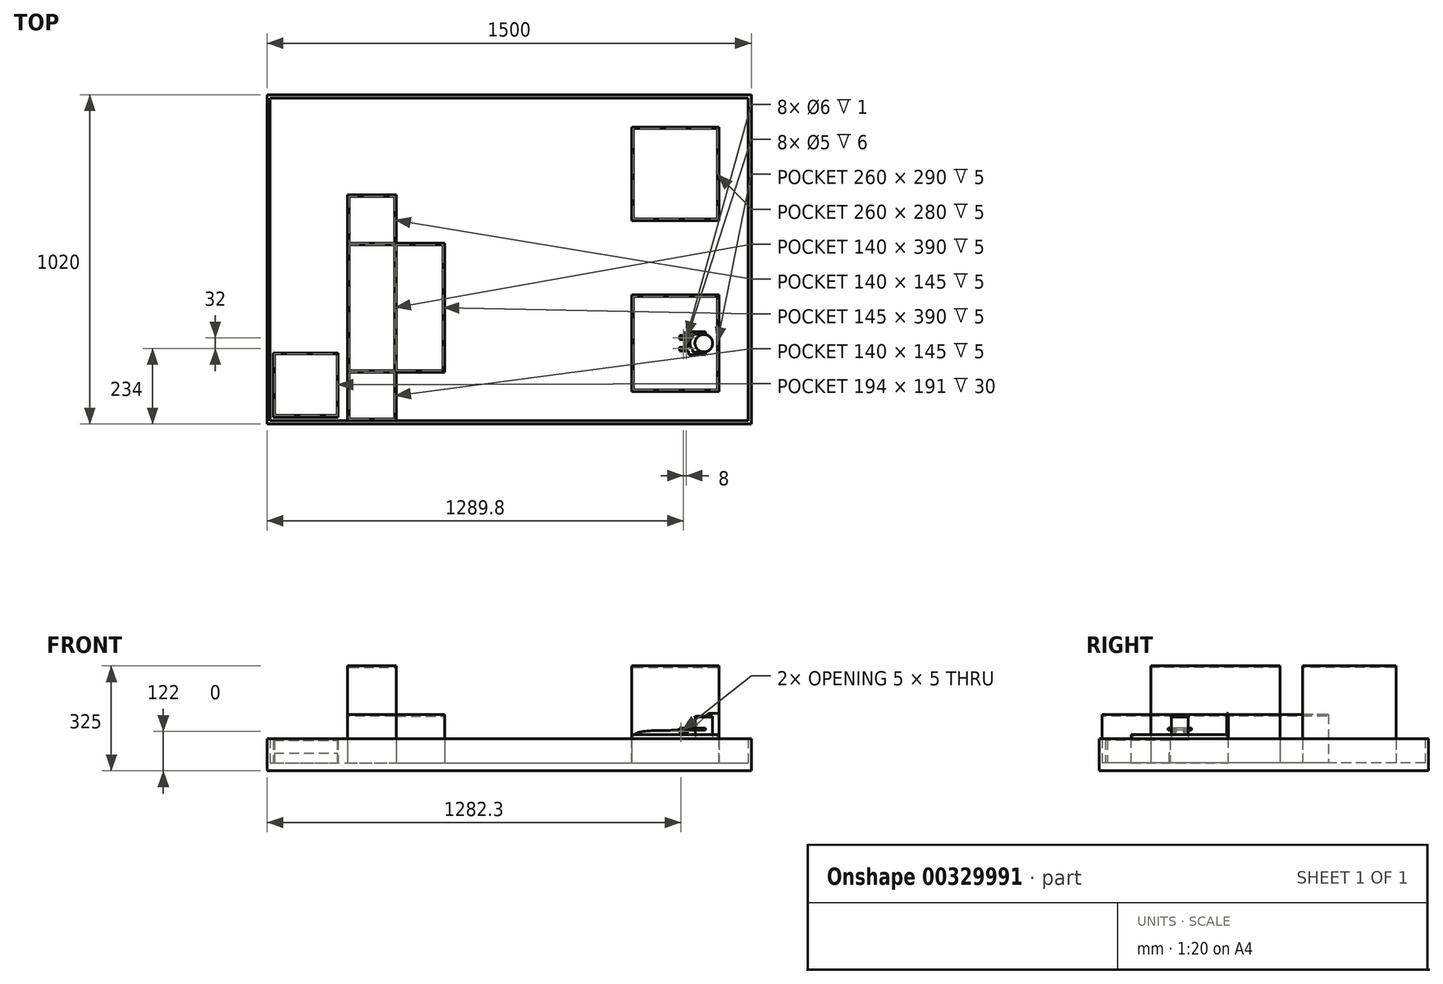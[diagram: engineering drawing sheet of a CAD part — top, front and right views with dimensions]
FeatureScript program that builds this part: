
annotation { "Feature Type Name" : "Feature", "Feature Type Description" : "" }
export const myFeature = defineFeature(function(context is Context, id is Id, definition is map)
    precondition{}
    {
        {
            var Q0;
            Q0=qCreatedBy(makeId("Top.planeOp"),FACE);
            var sketch = newSketch(context, id + "F0", { "sketchPlane" : qUnion([Q0])});
            skCircle(sketch, "E0", {"center": v(0, 0) * mm, "radius": 27.2 * mm});
            skSolve(sketch);
        }
        {
            var Q0;
            Q0=qSketchRegion(id+"F0",true);
            extrude(context, id + "F1", {"entities" : qUnion([Q0]), "depth" : 2.83 * mm});
        }
        {
            var Q0;
            Q0=makeQuery(id+"F1.opExtrude","CAP_FACE",FACE,{"disambiguationData":[OSD([sQuery(id+"F0.wireOp",EDGE,"E0")])],"isStart":false});
            var sketch = newSketch(context, id + "F2", { "sketchPlane" : qUnion([Q0])});
            skCircle(sketch, "E1", {"center": v(0, 0) * mm, "radius": 26.4 * mm});
            skSolve(sketch);
        }
        {
            var Q0;
            Q0=qSketchRegion(id+"F2",true);
            extrude(context, id + "F3", {"entities" : qUnion([Q0]), "operationType" : NewBodyOperationType.ADD, "depth" : 67.36 * mm});
        }
        {
            var Q0;
            Q0=makeQuery(id+"F3.opExtrude","CAP_FACE",FACE,{"disambiguationData":[OSD([sQuery(id+"F2.wireOp",EDGE,"E1")])],"isStart":false});
            var sketch = newSketch(context, id + "F4", { "sketchPlane" : qUnion([Q0])});
            skCircle(sketch, "E2", {"center": v(0, 0) * mm, "radius": 27.2 * mm});
            skSolve(sketch);
        }
        {
            var Q0;
            Q0=qSketchRegion(id+"F4",true);
            extrude(context, id + "F5", {"entities" : qUnion([Q0]), "operationType" : NewBodyOperationType.ADD, "depth" : 2.83 * mm});
        }
        {
            var Q0;
            Q0=makeQuery(id+"F5.opExtrude","CAP_FACE",FACE,{"disambiguationData":[OSD([sQuery(id+"F4.wireOp",EDGE,"E2")])],"isStart":false});
            var sketch = newSketch(context, id + "F6", { "sketchPlane" : qUnion([Q0])});
            skSolve(sketch);
        }
        {
            var Q0;
            Q0=qCreatedBy(makeId("Top.planeOp"),FACE);
            cPlane(context, id + "F7", {"entities" : qUnion([Q0]), "cplaneType" : CPlaneType.OFFSET, "offset" : 25 * mm, "width" : 150 * mm, "height" : 150 * mm});
        }
        {
            var Q0;
            Q0=makeQuery(id+"F6.imprint","IMPRINT",FACE,{"disambiguationData":[TD([[makeQuery(id+"F6.imprint","IMPRINT",EDGE,{"derivedFrom":makeQuery(id+"F5.opExtrude","CAP_EDGE",EDGE,{"disambiguationData":[OSD([sQuery(id+"F4.wireOp",EDGE,"E2")])],"isStart":false})}),1.0]])]});
            var sketch = newSketch(context, id + "F8", { "sketchPlane" : qUnion([Q0])});
            skSolve(sketch);
        }
        {
            var Q0;
            Q0=qCreatedBy(makeId("Top.planeOp"),FACE);
            var sketch = newSketch(context, id + "F9", { "sketchPlane" : qUnion([Q0])});
            skLineSegment(sketch, "E3.bottom", {"start": v(-222.8, -150) * mm, "end": v(47.2, -150) * mm});
            skLineSegment(sketch, "E3.top", {"start": v(-222.8, 150) * mm, "end": v(47.2, 150) * mm});
            skLineSegment(sketch, "E3.left", {"start": v(-222.8, -150) * mm, "end": v(-222.8, 150) * mm});
            skLineSegment(sketch, "E3.right", {"start": v(47.2, -150) * mm, "end": v(47.2, 150) * mm});
            skSolve(sketch);
        }
        {
            var Q0;
            Q0=qSketchRegion(id+"F9",true);
            extrude(context, id + "F10", {"entities" : qUnion([Q0]), "oppositeDirection" : true, "depth" : 72 * mm});
        }
        {
            var Q0;
            Q0=makeQuery(id+"F10.opExtrude","CAP_FACE",FACE,{"disambiguationData":[OSD([sQuery(id+"F9.wireOp",EDGE,"E3.bottom"),sQuery(id+"F9.wireOp",EDGE,"E3.top"),sQuery(id+"F9.wireOp",EDGE,"E3.left"),sQuery(id+"F9.wireOp",EDGE,"E3.right")])],"isStart":true});
            var sketch = newSketch(context, id + "F11", { "sketchPlane" : qUnion([Q0])});
            skLineSegment(sketch, "E4.bottom", {"start": v(-222.8, -150) * mm, "end": v(47.2, -150) * mm});
            skLineSegment(sketch, "E4.top", {"start": v(-222.8, -145) * mm, "end": v(42.2, -145) * mm});
            skLineSegment(sketch, "E4.left", {"start": v(-222.8, -150) * mm, "end": v(-222.8, -145) * mm});
            skLineSegment(sketch, "E5.bottom", {"start": v(47.2, 150) * mm, "end": v(42.2, 150) * mm});
            skLineSegment(sketch, "E5.left", {"start": v(47.2, 150) * mm, "end": v(47.2, -150) * mm});
            skLineSegment(sketch, "E5.right", {"start": v(42.2, 150) * mm, "end": v(42.2, -145) * mm});
            skSolve(sketch);
        }
        {
            var Q0;
            Q0=qSketchRegion(id+"F11",true);
            extrude(context, id + "F12", {"entities" : qUnion([Q0]), "operationType" : NewBodyOperationType.ADD, "depth" : 15 * mm});
        }
        {
            var Q0;
            Q0=makeQuery(id+"F12.boolean.opBoolean","MERGE",FACE,{"derivedFrom":[makeQuery(id+"F10.opExtrude","SWEPT_FACE",FACE,{"disambiguationData":[OSD([sQuery(id+"F9.wireOp",EDGE,"E3.top")])]}),makeQuery(id+"F12.opExtrude","SWEPT_FACE",FACE,{"disambiguationData":[OSD([sQuery(id+"F11.wireOp",EDGE,"E5.bottom")])]})]});
            var sketch = newSketch(context, id + "F13", { "sketchPlane" : qUnion([Q0])});
            skLineSegment(sketch, "E6", {"start": v(-47.2, 81.36) * mm, "end": v(-21.31, 81.36) * mm});
            skFitSpline(sketch, "E7", {"points": [v(-21.31, 81.36) * mm, v(15.24, 52.01) * mm, v(114.14, 28.17) * mm, v(222.8, 0) * mm], "startDerivative": vector(181.02, 0.3) * mm, "endDerivative": vector(-1.73, -239.85) * mm});
            skLineSegment(sketch, "E8", {"start": v(-47.2, 81.36) * mm, "end": v(-47.2, -72) * mm});
            skLineSegment(sketch, "E9", {"start": v(-47.2, -72) * mm, "end": v(222.8, -72) * mm});
            skLineSegment(sketch, "E10", {"start": v(222.8, -72) * mm, "end": v(222.8, 0) * mm});
            skSolve(sketch);
        }
        {
            var Q0;
            Q0=qSketchRegion(id+"F13",true);
            extrude(context, id + "F14", {"entities" : qUnion([Q0]), "operationType" : NewBodyOperationType.ADD, "oppositeDirection" : true, "depth" : 5 * mm});
        }
        {
            var Q0;
            Q0=makeQuery(id+"F10.opExtrude","CAP_FACE",FACE,{"disambiguationData":[OSD([sQuery(id+"F9.wireOp",EDGE,"E3.bottom"),sQuery(id+"F9.wireOp",EDGE,"E3.top"),sQuery(id+"F9.wireOp",EDGE,"E3.left"),sQuery(id+"F9.wireOp",EDGE,"E3.right")])],"isStart":true});
            var sketch = newSketch(context, id + "F15", { "sketchPlane" : qUnion([Q0])});
            skLineSegment(sketch, "E11.bottom", {"start": v(-222.8, 145) * mm, "end": v(-217.8, 145) * mm});
            skLineSegment(sketch, "E11.top", {"start": v(-222.8, -145) * mm, "end": v(-217.8, -145) * mm});
            skLineSegment(sketch, "E11.left", {"start": v(-222.8, 145) * mm, "end": v(-222.8, -145) * mm});
            skLineSegment(sketch, "E11.right", {"start": v(-217.8, 145) * mm, "end": v(-217.8, -145) * mm});
            skSolve(sketch);
        }
        {
            var Q0;
            Q0=qSketchRegion(id+"F15",true);
            extrude(context, id + "F16", {"entities" : qUnion([Q0]), "operationType" : NewBodyOperationType.ADD, "depth" : 5 * mm});
        }
        {
            var Q0;
            Q0=makeQuery(id+"F10.opExtrude","CAP_FACE",FACE,{"disambiguationData":[OSD([sQuery(id+"F9.wireOp",EDGE,"E3.bottom"),sQuery(id+"F9.wireOp",EDGE,"E3.top"),sQuery(id+"F9.wireOp",EDGE,"E3.left"),sQuery(id+"F9.wireOp",EDGE,"E3.right")])],"isStart":false});
            var sketch = newSketch(context, id + "F17", { "sketchPlane" : qUnion([Q0])});
            skLineSegment(sketch, "E12.bottom", {"start": v(147.2, 250) * mm, "end": v(-1352.8, 250) * mm});
            skLineSegment(sketch, "E12.top", {"start": v(147.2, -770) * mm, "end": v(-1352.8, -770) * mm});
            skLineSegment(sketch, "E12.left", {"start": v(147.2, 250) * mm, "end": v(147.2, -770) * mm});
            skLineSegment(sketch, "E12.right", {"start": v(-1352.8, 250) * mm, "end": v(-1352.8, -770) * mm});
            skSolve(sketch);
        }
        {
            var Q0;
            Q0=qSketchRegion(id+"F17",true);
            extrude(context, id + "F18", {"entities" : qUnion([Q0]), "operationType" : NewBodyOperationType.ADD, "depth" : 25 * mm});
        }
        {
            var Q0;
            Q0=makeQuery(id+"F18.opExtrude","CAP_FACE",FACE,{"disambiguationData":[OSD([sQuery(id+"F17.wireOp",EDGE,"E12.bottom"),sQuery(id+"F17.wireOp",EDGE,"E12.top"),sQuery(id+"F17.wireOp",EDGE,"E12.left"),sQuery(id+"F17.wireOp",EDGE,"E12.right")])],"isStart":true});
            var sketch = newSketch(context, id + "F19", { "sketchPlane" : qUnion([Q0])});
            skLineSegment(sketch, "E13.bottom", {"start": v(-222.8, 670) * mm, "end": v(47.2, 670) * mm});
            skLineSegment(sketch, "E13.top", {"start": v(-222.8, 380) * mm, "end": v(47.2, 380) * mm});
            skLineSegment(sketch, "E13.left", {"start": v(-222.8, 670) * mm, "end": v(-222.8, 380) * mm});
            skLineSegment(sketch, "E13.right", {"start": v(47.2, 670) * mm, "end": v(47.2, 380) * mm});
            skSolve(sketch);
        }
        {
            var Q0;
            Q0=qSketchRegion(id+"F19",true);
            extrude(context, id + "F20", {"entities" : qUnion([Q0]), "operationType" : NewBodyOperationType.ADD, "depth" : 300 * mm});
        }
        {
            var Q0;
            Q0=makeQuery(id+"F20.opExtrude","CAP_FACE",FACE,{"disambiguationData":[OSD([sQuery(id+"F19.wireOp",EDGE,"E13.bottom"),sQuery(id+"F19.wireOp",EDGE,"E13.top"),sQuery(id+"F19.wireOp",EDGE,"E13.left"),sQuery(id+"F19.wireOp",EDGE,"E13.right")])],"isStart":false});
            var sketch = newSketch(context, id + "F21", { "sketchPlane" : qUnion([Q0])});
            skLineSegment(sketch, "E14.bottom", {"start": v(-217.8, 665) * mm, "end": v(42.2, 665) * mm});
            skLineSegment(sketch, "E14.top", {"start": v(-217.8, 385) * mm, "end": v(42.2, 385) * mm});
            skLineSegment(sketch, "E14.left", {"start": v(-217.8, 665) * mm, "end": v(-217.8, 385) * mm});
            skLineSegment(sketch, "E14.right", {"start": v(42.2, 665) * mm, "end": v(42.2, 385) * mm});
            skSolve(sketch);
        }
        {
            var Q0;
            Q0=qSketchRegion(id+"F21",true);
            extrude(context, id + "F22", {"entities" : qUnion([Q0]), "operationType" : NewBodyOperationType.REMOVE, "oppositeDirection" : true, "depth" : 5 * mm});
        }
        {
            var Q0;
            Q0=makeQuery(id+"F18.opExtrude","CAP_FACE",FACE,{"disambiguationData":[OSD([sQuery(id+"F17.wireOp",EDGE,"E12.bottom"),sQuery(id+"F17.wireOp",EDGE,"E12.top"),sQuery(id+"F17.wireOp",EDGE,"E12.left"),sQuery(id+"F17.wireOp",EDGE,"E12.right")])],"isStart":true});
            var sketch = newSketch(context, id + "F23", { "sketchPlane" : qUnion([Q0])});
            skLineSegment(sketch, "E15.bottom", {"start": v(-1352.8, 770) * mm, "end": v(147.2, 770) * mm});
            skLineSegment(sketch, "E15.top", {"start": v(-1352.8, -250) * mm, "end": v(147.2, -250) * mm});
            skLineSegment(sketch, "E15.left", {"start": v(-1352.8, 770) * mm, "end": v(-1352.8, -250) * mm});
            skLineSegment(sketch, "E15.right", {"start": v(147.2, 770) * mm, "end": v(147.2, -250) * mm});
            skLineSegment(sketch, "E16.bottom", {"start": v(-1342.8, 760) * mm, "end": v(137.2, 760) * mm});
            skLineSegment(sketch, "E16.top", {"start": v(-1342.8, -240) * mm, "end": v(137.2, -240) * mm});
            skLineSegment(sketch, "E16.left", {"start": v(-1342.8, 760) * mm, "end": v(-1342.8, -240) * mm});
            skLineSegment(sketch, "E16.right", {"start": v(137.2, 760) * mm, "end": v(137.2, -240) * mm});
            skSolve(sketch);
        }
        {
            var Q0;
            Q0=qSketchRegion(id+"F23",true);
            extrude(context, id + "F24", {"entities" : qUnion([Q0]), "operationType" : NewBodyOperationType.ADD, "depth" : 75 * mm});
        }
        {
            var Q0;
            Q0=makeQuery(id+"F18.opExtrude","CAP_FACE",FACE,{"disambiguationData":[OSD([sQuery(id+"F17.wireOp",EDGE,"E12.bottom"),sQuery(id+"F17.wireOp",EDGE,"E12.top"),sQuery(id+"F17.wireOp",EDGE,"E12.left"),sQuery(id+"F17.wireOp",EDGE,"E12.right")])],"isStart":true});
            var sketch = newSketch(context, id + "F25", { "sketchPlane" : qUnion([Q0])});
            skLineSegment(sketch, "E17.bottom", {"start": v(-1102.8, 460) * mm, "end": v(-952.8, 460) * mm});
            skLineSegment(sketch, "E17.top", {"start": v(-1102.8, -240) * mm, "end": v(-952.8, -240) * mm});
            skLineSegment(sketch, "E17.left", {"start": v(-1102.8, 460) * mm, "end": v(-1102.8, -240) * mm});
            skLineSegment(sketch, "E17.right", {"start": v(-952.8, 460) * mm, "end": v(-952.8, 310) * mm});
            skLineSegment(sketch, "E18.bottom", {"start": v(-952.8, 310) * mm, "end": v(-802.8, 310) * mm});
            skLineSegment(sketch, "E18.top", {"start": v(-952.8, -90) * mm, "end": v(-802.8, -90) * mm});
            skLineSegment(sketch, "E18.right", {"start": v(-802.8, 310) * mm, "end": v(-802.8, -90) * mm});
            skLineSegment(sketch, "E19.trimOffspring", {"start": v(-952.8, -90) * mm, "end": v(-952.8, -240) * mm});
            skSolve(sketch);
        }
        {
            var Q0;
            Q0=qSketchRegion(id+"F25",true);
            extrude(context, id + "F26", {"entities" : qUnion([Q0]), "operationType" : NewBodyOperationType.ADD, "depth" : 150 * mm});
        }
        {
            var Q0;
            Q0=makeQuery(id+"F26.opExtrude","CAP_FACE",FACE,{"disambiguationData":[OSD([sQuery(id+"F25.wireOp",EDGE,"E17.bottom"),sQuery(id+"F25.wireOp",EDGE,"E17.top"),sQuery(id+"F25.wireOp",EDGE,"E17.left"),sQuery(id+"F25.wireOp",EDGE,"E17.right"),sQuery(id+"F25.wireOp",EDGE,"E18.bottom"),sQuery(id+"F25.wireOp",EDGE,"E18.top"),sQuery(id+"F25.wireOp",EDGE,"E18.right"),sQuery(id+"F25.wireOp",EDGE,"E19.trimOffspring")])],"isStart":false});
            var sketch = newSketch(context, id + "F27", { "sketchPlane" : qUnion([Q0])});
            skLineSegment(sketch, "E20.bottom", {"start": v(-952.8, 310) * mm, "end": v(-1102.8, 310) * mm});
            skLineSegment(sketch, "E20.top", {"start": v(-952.8, -90) * mm, "end": v(-1102.8, -90) * mm});
            skLineSegment(sketch, "E20.left", {"start": v(-952.8, 310) * mm, "end": v(-952.8, -90) * mm});
            skLineSegment(sketch, "E20.right", {"start": v(-1102.8, 310) * mm, "end": v(-1102.8, -90) * mm});
            skSolve(sketch);
        }
        {
            var Q0;
            Q0=qSketchRegion(id+"F27",true);
            extrude(context, id + "F28", {"entities" : qUnion([Q0]), "operationType" : NewBodyOperationType.ADD, "depth" : 150 * mm});
        }
        {
            var Q0;
            Q0=makeQuery(id+"F28.opExtrude","CAP_FACE",FACE,{"disambiguationData":[OSD([sQuery(id+"F27.wireOp",EDGE,"E20.bottom"),sQuery(id+"F27.wireOp",EDGE,"E20.top"),sQuery(id+"F27.wireOp",EDGE,"E20.left"),sQuery(id+"F27.wireOp",EDGE,"E20.right")])],"isStart":false});
            var sketch = newSketch(context, id + "F29", { "sketchPlane" : qUnion([Q0])});
            skLineSegment(sketch, "E21.bottom", {"start": v(-1097.8, 305) * mm, "end": v(-957.8, 305) * mm});
            skLineSegment(sketch, "E21.top", {"start": v(-1097.8, -85) * mm, "end": v(-957.8, -85) * mm});
            skLineSegment(sketch, "E21.left", {"start": v(-1097.8, 305) * mm, "end": v(-1097.8, -85) * mm});
            skLineSegment(sketch, "E21.right", {"start": v(-957.8, 305) * mm, "end": v(-957.8, -85) * mm});
            skSolve(sketch);
        }
        {
            var Q0;
            Q0=qSketchRegion(id+"F29",true);
            extrude(context, id + "F30", {"entities" : qUnion([Q0]), "operationType" : NewBodyOperationType.REMOVE, "oppositeDirection" : true, "depth" : 5 * mm});
        }
        {
            var Q0;
            {var subQ0=sQuery(id+"F25.wireOp",EDGE,"E17.left");var subQ1=sQuery(id+"F25.wireOp",EDGE,"E18.bottom");var subQ2=sQuery(id+"F25.wireOp",EDGE,"E17.right");var subQ3=sQuery(id+"F25.wireOp",EDGE,"E17.bottom");var subQ4=makeQuery(id+"F26.opExtrude","CAP_FACE",FACE,{"disambiguationData":[OSD([subQ3,sQuery(id+"F25.wireOp",EDGE,"E17.top"),subQ0,subQ2,subQ1,sQuery(id+"F25.wireOp",EDGE,"E18.top"),sQuery(id+"F25.wireOp",EDGE,"E18.right"),sQuery(id+"F25.wireOp",EDGE,"E19.trimOffspring")])],"isStart":false});Q0=makeQuery(id+"F28.boolean.opBoolean","SPLIT",FACE,{"disambiguationData":[TD([makeQuery(id+"F26.opExtrude","SWEPT_FACE",FACE,{"disambiguationData":[OSD([subQ3])]})])],"derivedFrom":subQ4});}
            var sketch = newSketch(context, id + "F31", { "sketchPlane" : qUnion([Q0])});
            skLineSegment(sketch, "E22.bottom", {"start": v(-1097.8, 455) * mm, "end": v(-957.8, 455) * mm});
            skLineSegment(sketch, "E22.top", {"start": v(-1097.8, 310) * mm, "end": v(-957.8, 310) * mm});
            skLineSegment(sketch, "E22.left", {"start": v(-1097.8, 455) * mm, "end": v(-1097.8, 310) * mm});
            skLineSegment(sketch, "E22.right", {"start": v(-957.8, 455) * mm, "end": v(-957.8, 310) * mm});
            skLineSegment(sketch, "E23.bottom", {"start": v(-952.8, 305) * mm, "end": v(-807.8, 305) * mm});
            skLineSegment(sketch, "E23.top", {"start": v(-952.8, -85) * mm, "end": v(-807.8, -85) * mm});
            skLineSegment(sketch, "E23.left", {"start": v(-952.8, 305) * mm, "end": v(-952.8, -85) * mm});
            skLineSegment(sketch, "E23.right", {"start": v(-807.8, 305) * mm, "end": v(-807.8, -85) * mm});
            skLineSegment(sketch, "E24.bottom", {"start": v(-1097.8, -90) * mm, "end": v(-957.8, -90) * mm});
            skLineSegment(sketch, "E24.top", {"start": v(-1097.8, -235) * mm, "end": v(-957.8, -235) * mm});
            skLineSegment(sketch, "E24.left", {"start": v(-1097.8, -90) * mm, "end": v(-1097.8, -235) * mm});
            skLineSegment(sketch, "E24.right", {"start": v(-957.8, -90) * mm, "end": v(-957.8, -235) * mm});
            skSolve(sketch);
        }
        {
            var Q0;
            Q0=qSketchRegion(id+"F31",true);
            extrude(context, id + "F32", {"entities" : qUnion([Q0]), "operationType" : NewBodyOperationType.REMOVE, "oppositeDirection" : true, "depth" : 5 * mm});
        }
        {
            var Q0;
            Q0=qCreatedBy(id+"F7.planeOp",FACE);
            var sketch = newSketch(context, id + "F33", { "sketchPlane" : qUnion([Q0])});
            skLineSegment(sketch, "E25", {"start": v(0, 0) * mm, "end": v(-90, 0) * mm, "construction": true});
            skLineSegment(sketch, "E26.bottom", {"start": v(-74.5, -12) * mm, "end": v(-55, -12) * mm});
            skLineSegment(sketch, "E26.top", {"start": v(-74.5, -20) * mm, "end": v(-55, -20) * mm});
            skLineSegment(sketch, "E26.left", {"start": v(-74.5, -12) * mm, "end": v(-74.5, -13) * mm});
            skPoint(sketch, "E27.visualSharp", {"position": v(-51, -12) * mm});
            skPoint(sketch, "E28.visualSharp", {"position": v(-51, -20) * mm});
            skCircle(sketch, "E29", {"center": v(-55, -16) * mm, "radius": 3 * mm});
            skLineSegment(sketch, "E30", {"start": v(-59, -3.98) * mm, "end": v(-59, -18.08) * mm, "construction": true});
            skCircle(sketch, "E31.MirrorC", {"center": v(-63, -16) * mm, "radius": 3 * mm});
            skLineSegment(sketch, "E32.bottom", {"start": v(-74.5, -13) * mm, "end": v(-65.65, -13) * mm});
            skLineSegment(sketch, "E32.top", {"start": v(-74.5, -19) * mm, "end": v(-65.65, -19) * mm});
            skArc(sketch, "E33", {"start": v(-65.65, -13) * mm, "mid": v(-67, -16) * mm, "end": v(-65.65, -19) * mm});
            skLineSegment(sketch, "E34.trimOffspring", {"start": v(-74.5, -19) * mm, "end": v(-74.5, -20) * mm});
            skArc(sketch, "E35.trimOffspring", {"start": v(-55, -20) * mm, "mid": v(-51, -16) * mm, "end": v(-55, -12) * mm});
            skLineSegment(sketch, "E36.MirrorCS", {"start": v(-74.5, 12) * mm, "end": v(-74.5, 13) * mm});
            skLineSegment(sketch, "E37.MirrorCS", {"start": v(-74.5, 19) * mm, "end": v(-74.5, 20) * mm});
            skPoint(sketch, "E38.MirrorP", {"position": v(-51, 12) * mm});
            skLineSegment(sketch, "E39.MirrorCS", {"start": v(-74.5, 12) * mm, "end": v(-55, 12) * mm});
            skPoint(sketch, "E40.MirrorP", {"position": v(-51, 20) * mm});
            skArc(sketch, "E41.MirrorCS", {"start": v(-65.65, 13) * mm, "mid": v(-67, 16) * mm, "end": v(-65.65, 19) * mm});
            skArc(sketch, "E42.MirrorCS", {"start": v(-55, 20) * mm, "mid": v(-51, 16) * mm, "end": v(-55, 12) * mm});
            skLineSegment(sketch, "E43.MirrorCS", {"start": v(-74.5, 20) * mm, "end": v(-55, 20) * mm});
            skCircle(sketch, "E44.MirrorC", {"center": v(-55, 16) * mm, "radius": 3 * mm});
            skCircle(sketch, "E45.MirrorC", {"center": v(-63, 16) * mm, "radius": 3 * mm});
            skLineSegment(sketch, "E46.MirrorCS", {"start": v(-74.5, 19) * mm, "end": v(-65.65, 19) * mm});
            skLineSegment(sketch, "E47.MirrorCS", {"start": v(-74.5, 13) * mm, "end": v(-65.65, 13) * mm});
            skSolve(sketch);
        }
        {
            var Q0;
            Q0=qSketchRegion(id+"F33",true);
            var Q1;
            Q1=qSketchRegion(id+"F36",true);
            extrude(context, id + "F34", {"entities" : qUnion([Q0, Q1]), "endBound" : BoundingType.SYMMETRIC, "depth" : 8 * mm});
        }
        {
            var Q0;
            Q0=makeQuery(id+"F34.opExtrude","CAP_EDGE",EDGE,{"disambiguationData":[OSD([sQuery(id+"F33.wireOp",EDGE,"E34.trimOffspring")])],"isStart":false});
            var Q1;
            Q1=makeQuery(id+"F34.opExtrude","CAP_EDGE",EDGE,{"disambiguationData":[OSD([sQuery(id+"F33.wireOp",EDGE,"E26.left")])],"isStart":false});
            var Q2;
            Q2=makeQuery(id+"F34.opExtrude","CAP_EDGE",EDGE,{"disambiguationData":[OSD([sQuery(id+"F33.wireOp",EDGE,"E34.trimOffspring")])],"isStart":true});
            var Q3;
            Q3=makeQuery(id+"F34.opExtrude","CAP_EDGE",EDGE,{"disambiguationData":[OSD([sQuery(id+"F33.wireOp",EDGE,"E26.left")])],"isStart":true});
            var Q4;
            Q4=makeQuery(id+"F34.opExtrude","CAP_EDGE",EDGE,{"disambiguationData":[OSD([sQuery(id+"F33.wireOp",EDGE,"E36.MirrorCS")])],"isStart":false});
            var Q5;
            Q5=makeQuery(id+"F34.opExtrude","CAP_EDGE",EDGE,{"disambiguationData":[OSD([sQuery(id+"F33.wireOp",EDGE,"E37.MirrorCS")])],"isStart":false});
            var Q6;
            Q6=makeQuery(id+"F34.opExtrude","CAP_EDGE",EDGE,{"disambiguationData":[OSD([sQuery(id+"F33.wireOp",EDGE,"E37.MirrorCS")])],"isStart":true});
            var Q7;
            Q7=makeQuery(id+"F34.opExtrude","CAP_EDGE",EDGE,{"disambiguationData":[OSD([sQuery(id+"F33.wireOp",EDGE,"E36.MirrorCS")])],"isStart":true});
            fillet(context, id + "F35", {"entities" : qUnion([Q0, Q1, Q2, Q3, Q4, Q5, Q6, Q7]), "radius" : 4 * mm, "tangentPropagation" : true, "allowEdgeOverflow" : false});
        }
        {
            var Q0;
            Q0=makeQuery(id+"F34.opExtrude","SWEPT_FACE",FACE,{"disambiguationData":[OSD([sQuery(id+"F33.wireOp",EDGE,"E26.top")])]});
            var sketch = newSketch(context, id + "F36", { "sketchPlane" : qUnion([Q0])});
            skCircle(sketch, "E48", {"center": v(-70.5, 25) * mm, "radius": 3 * mm});
            skSolve(sketch);
        }
        {
            var Q0;
            Q0=qSketchRegion(id+"F36",true);
            var Q1;
            Q1=makeQuery(id+"F34.opExtrude","SWEPT_FACE",FACE,{"disambiguationData":[OSD([sQuery(id+"F33.wireOp",EDGE,"E26.bottom")])]});
            extrude(context, id + "F37", {"entities" : qUnion([Q0]), "operationType" : NewBodyOperationType.ADD, "endBound" : BoundingType.UP_TO_SURFACE, "oppositeDirection" : true, "endBoundEntityFace" : qUnion([Q1]), "depth" : 25 * mm});
        }
        {
            var Q0;
            Q0=makeQuery(id+"F34.opExtrude","SWEPT_FACE",FACE,{"disambiguationData":[OSD([sQuery(id+"F33.wireOp",EDGE,"E43.MirrorCS")])]});
            var sketch = newSketch(context, id + "F38", { "sketchPlane" : qUnion([Q0])});
            skCircle(sketch, "E49", {"center": v(70.5, 25) * mm, "radius": 3 * mm});
            skSolve(sketch);
        }
        {
            var Q0;
            Q0=qSketchRegion(id+"F38",true);
            var Q1;
            Q1=makeQuery(id+"F34.opExtrude","SWEPT_FACE",FACE,{"disambiguationData":[OSD([sQuery(id+"F33.wireOp",EDGE,"E39.MirrorCS")])]});
            extrude(context, id + "F39", {"entities" : qUnion([Q0]), "operationType" : NewBodyOperationType.ADD, "endBound" : BoundingType.UP_TO_SURFACE, "oppositeDirection" : true, "endBoundEntityFace" : qUnion([Q1]), "depth" : 25 * mm});
        }
        {
            var Q0;
            Q0=qCreatedBy(id+"F7.planeOp",FACE);
            var sketch = newSketch(context, id + "F40", { "sketchPlane" : qUnion([Q0])});
            skCircle(sketch, "E50", {"center": v(-55, 16) * mm, "radius": 3 * mm});
            skCircle(sketch, "E51", {"center": v(-63, 16) * mm, "radius": 2.5 * mm});
            skCircle(sketch, "E52", {"center": v(-63, 16) * mm, "radius": 3 * mm});
            skCircle(sketch, "E53", {"center": v(-55, 16) * mm, "radius": 2.5 * mm});
            skSolve(sketch);
        }
        {
            var Q0;
            Q0=qSketchRegion(id+"F40",true);
            extrude(context, id + "F41", {"entities" : qUnion([Q0]), "operationType" : NewBodyOperationType.ADD, "endBound" : BoundingType.SYMMETRIC, "depth" : 6 * mm});
        }
        {
            var Q0;
            Q0=qCreatedBy(id+"F7.planeOp",FACE);
            var sketch = newSketch(context, id + "F42", { "sketchPlane" : qUnion([Q0])});
            skCircle(sketch, "E54", {"center": v(-63, -16) * mm, "radius": 2.5 * mm});
            skCircle(sketch, "E55", {"center": v(-63, -16) * mm, "radius": 3 * mm});
            skCircle(sketch, "E56", {"center": v(-55, -16) * mm, "radius": 2.5 * mm});
            skCircle(sketch, "E57", {"center": v(-55, -16) * mm, "radius": 3 * mm});
            skSolve(sketch);
        }
        {
            var Q0;
            Q0=qSketchRegion(id+"F42",true);
            extrude(context, id + "F43", {"entities" : qUnion([Q0]), "operationType" : NewBodyOperationType.ADD, "endBound" : BoundingType.SYMMETRIC, "depth" : 6 * mm});
        }
        {
            var Q0;
            Q0=makeQuery(id+"F34.opExtrude","SWEPT_FACE",FACE,{"disambiguationData":[OSD([sQuery(id+"F33.wireOp",EDGE,"E43.MirrorCS")])]});
            var sketch = newSketch(context, id + "F44", { "sketchPlane" : qUnion([Q0])});
            skArc(sketch, "E58", {"start": v(71.5, 27.3) * mm, "mid": v(70.5, 27.5) * mm, "end": v(69.5, 27.3) * mm});
            skLineSegment(sketch, "E59.bottom", {"start": v(68.2, 26) * mm, "end": v(69.5, 26) * mm});
            skLineSegment(sketch, "E59.top", {"start": v(68.2, 24) * mm, "end": v(69.5, 24) * mm});
            skLineSegment(sketch, "E60.left", {"start": v(71.5, 27.3) * mm, "end": v(71.5, 26) * mm});
            skLineSegment(sketch, "E60.right", {"start": v(69.5, 27.3) * mm, "end": v(69.5, 26) * mm});
            skPoint(sketch, "E61.orphan", {"position": v(69.5, 27.8) * mm});
            skPoint(sketch, "E62.orphan", {"position": v(71.5, 27.8) * mm});
            skArc(sketch, "E63.trimOffspring", {"start": v(68.2, 26) * mm, "mid": v(68, 25) * mm, "end": v(68.2, 24) * mm});
            skPoint(sketch, "E59.left.start.orphan", {"position": v(67.32, 26) * mm});
            skPoint(sketch, "E64.orphan", {"position": v(67.32, 24) * mm});
            skArc(sketch, "E65.trimOffspring", {"start": v(69.5, 22.7) * mm, "mid": v(70.5, 22.5) * mm, "end": v(71.5, 22.7) * mm});
            skLineSegment(sketch, "E66.trimOffspring", {"start": v(69.5, 24) * mm, "end": v(69.5, 22.7) * mm});
            skLineSegment(sketch, "E67.trimOffspring", {"start": v(71.5, 26) * mm, "end": v(72.8, 26) * mm});
            skLineSegment(sketch, "E68.trimOffspring", {"start": v(71.5, 24) * mm, "end": v(71.5, 22.7) * mm});
            skLineSegment(sketch, "E69.trimOffspring", {"start": v(71.5, 24) * mm, "end": v(72.8, 24) * mm});
            skPoint(sketch, "E60.top.end.orphan", {"position": v(69.5, 22.2) * mm});
            skPoint(sketch, "E70.orphan", {"position": v(71.5, 22.2) * mm});
            skPoint(sketch, "E59.right.end.orphan", {"position": v(73.68, 24) * mm});
            skPoint(sketch, "E71.orphan", {"position": v(73.68, 26) * mm});
            skArc(sketch, "E72.trimOffspring", {"start": v(72.8, 24) * mm, "mid": v(73, 25) * mm, "end": v(72.8, 26) * mm});
            skSolve(sketch);
        }
        {
            var Q0;
            Q0=qSketchRegion(id+"F44",true);
            extrude(context, id + "F45", {"entities" : qUnion([Q0]), "operationType" : NewBodyOperationType.REMOVE, "endBound" : BoundingType.THROUGH_ALL, "oppositeDirection" : true, "depth" : 25 * mm});
        }
        {
            var Q0;
            Q0=makeQuery(id+"F18.opExtrude","CAP_FACE",FACE,{"disambiguationData":[OSD([sQuery(id+"F17.wireOp",EDGE,"E12.bottom"),sQuery(id+"F17.wireOp",EDGE,"E12.top"),sQuery(id+"F17.wireOp",EDGE,"E12.left"),sQuery(id+"F17.wireOp",EDGE,"E12.right")])],"isStart":true});
            var sketch = newSketch(context, id + "F46", { "sketchPlane" : qUnion([Q0])});
            skLineSegment(sketch, "E73.bottom", {"start": v(-1332.8, -30) * mm, "end": v(-1132.8, -30) * mm});
            skLineSegment(sketch, "E73.top", {"start": v(-1332.8, -230) * mm, "end": v(-1132.8, -230) * mm});
            skLineSegment(sketch, "E73.left", {"start": v(-1332.8, -30) * mm, "end": v(-1332.8, -230) * mm});
            skLineSegment(sketch, "E73.right", {"start": v(-1132.8, -30) * mm, "end": v(-1132.8, -230) * mm});
            skLineSegment(sketch, "E74.bottom", {"start": v(-1329.8, -33) * mm, "end": v(-1135.8, -33) * mm});
            skLineSegment(sketch, "E74.top", {"start": v(-1329.8, -224) * mm, "end": v(-1135.8, -224) * mm});
            skLineSegment(sketch, "E74.left", {"start": v(-1329.8, -33) * mm, "end": v(-1329.8, -224) * mm});
            skLineSegment(sketch, "E74.right", {"start": v(-1135.8, -33) * mm, "end": v(-1135.8, -224) * mm});
            skSolve(sketch);
        }
        {
            var Q0;
            Q0=qSketchRegion(id+"F46",true);
            extrude(context, id + "F47", {"entities" : qUnion([Q0]), "operationType" : NewBodyOperationType.ADD, "depth" : 30 * mm});
        }
        {
            var Q0;
            Q0=makeQuery(id+"F47.opExtrude","CAP_FACE",FACE,{"disambiguationData":[OSD([sQuery(id+"F46.wireOp",EDGE,"E73.bottom"),sQuery(id+"F46.wireOp",EDGE,"E73.top"),sQuery(id+"F46.wireOp",EDGE,"E73.left"),sQuery(id+"F46.wireOp",EDGE,"E73.right"),sQuery(id+"F46.wireOp",EDGE,"E74.bottom"),sQuery(id+"F46.wireOp",EDGE,"E74.top"),sQuery(id+"F46.wireOp",EDGE,"E74.left"),sQuery(id+"F46.wireOp",EDGE,"E74.right")])],"isStart":false});
            var sketch = newSketch(context, id + "F48", { "sketchPlane" : qUnion([Q0])});
            skLineSegment(sketch, "E75.bottom", {"start": v(-1332.8, -30) * mm, "end": v(-1329.8, -30) * mm});
            skLineSegment(sketch, "E75.top", {"start": v(-1332.8, -230) * mm, "end": v(-1329.8, -230) * mm});
            skLineSegment(sketch, "E75.left", {"start": v(-1332.8, -30) * mm, "end": v(-1332.8, -230) * mm});
            skLineSegment(sketch, "E75.right", {"start": v(-1329.8, -30) * mm, "end": v(-1329.8, -224) * mm});
            skLineSegment(sketch, "E76.bottom", {"start": v(-1329.8, -230) * mm, "end": v(-1135.8, -230) * mm});
            skLineSegment(sketch, "E76.top", {"start": v(-1329.8, -224) * mm, "end": v(-1135.8, -224) * mm});
            skLineSegment(sketch, "E77.bottom", {"start": v(-1135.8, -230) * mm, "end": v(-1132.8, -230) * mm});
            skLineSegment(sketch, "E77.top", {"start": v(-1135.8, -30) * mm, "end": v(-1132.8, -30) * mm});
            skLineSegment(sketch, "E77.left", {"start": v(-1135.8, -224) * mm, "end": v(-1135.8, -30) * mm});
            skLineSegment(sketch, "E77.right", {"start": v(-1132.8, -230) * mm, "end": v(-1132.8, -30) * mm});
            skSolve(sketch);
        }
        {
            var Q0;
            Q0=qSketchRegion(id+"F48",true);
            extrude(context, id + "F49", {"entities" : qUnion([Q0]), "operationType" : NewBodyOperationType.ADD, "depth" : 40 * mm});
        }
        {
            var Q0;
            Q0=makeQuery(id+"F34.opExtrude","CAP_FACE",FACE,{"disambiguationData":[OSD([sQuery(id+"F33.wireOp",EDGE,"E26.bottom"),sQuery(id+"F33.wireOp",EDGE,"E26.top"),sQuery(id+"F33.wireOp",EDGE,"E26.left"),sQuery(id+"F33.wireOp",EDGE,"E29"),sQuery(id+"F33.wireOp",EDGE,"E31.MirrorC"),sQuery(id+"F33.wireOp",EDGE,"E32.bottom"),sQuery(id+"F33.wireOp",EDGE,"E32.top"),sQuery(id+"F33.wireOp",EDGE,"E33"),sQuery(id+"F33.wireOp",EDGE,"E34.trimOffspring"),sQuery(id+"F33.wireOp",EDGE,"E35.trimOffspring")])],"isStart":false});
            var sketch = newSketch(context, id + "F50", { "sketchPlane" : qUnion([Q0])});
            skLineSegment(sketch, "E78", {"start": v(-74.28, 20) * mm, "end": v(-34.03, 20) * mm});
            skLineSegment(sketch, "E79", {"start": v(-34.03, 20.26) * mm, "end": v(-34.03, 20) * mm});
            skLineSegment(sketch, "E80", {"start": v(-34.03, -20) * mm, "end": v(-74.28, -20) * mm});
            skLineSegment(sketch, "E81", {"start": v(-74.28, -20) * mm, "end": v(-74.28, -12) * mm});
            skArc(sketch, "E82", {"start": v(-34.03, 20.26) * mm, "mid": v(-42.94, 0.13) * mm, "end": v(-34.03, -20) * mm});
            skLineSegment(sketch, "E83.trimOffspring", {"start": v(-34.03, -20) * mm, "end": v(-34.03, -20) * mm});
            skCircle(sketch, "E84", {"center": v(-63, 16) * mm, "radius": 2.5 * mm});
            skCircle(sketch, "E85", {"center": v(-55, 16) * mm, "radius": 2.5 * mm});
            skCircle(sketch, "E86", {"center": v(-63, -16) * mm, "radius": 2.5 * mm});
            skCircle(sketch, "E87", {"center": v(-55, -16) * mm, "radius": 2.5 * mm});
            skLineSegment(sketch, "E88.bottom", {"start": v(-74.28, 12) * mm, "end": v(-48.72, 12) * mm});
            skLineSegment(sketch, "E88.top", {"start": v(-74.28, -12) * mm, "end": v(-48.72, -12) * mm});
            skLineSegment(sketch, "E88.right", {"start": v(-48.72, 12) * mm, "end": v(-48.72, -12) * mm});
            skLineSegment(sketch, "E89.trimOffspring", {"start": v(-74.28, 12) * mm, "end": v(-74.28, 20) * mm});
            skSolve(sketch);
        }
        {
            var Q0;
            Q0 = qSketchRegion(id + "F50", true);
            extrude(context, id + "F51", {"entities" : qUnion([Q0]), "depth" : 6 * mm});
        }
        {
            var Q0;
            Q0=makeQuery(id+"F51.opExtrude","CAP_FACE",FACE,{"disambiguationData":[OSD([sQuery(id+"F50.wireOp",EDGE,"E78"),sQuery(id+"F50.wireOp",EDGE,"E80"),sQuery(id+"F50.wireOp",EDGE,"E81"),sQuery(id+"F50.wireOp",EDGE,"E82"),sQuery(id+"F50.wireOp",EDGE,"E84"),sQuery(id+"F50.wireOp",EDGE,"E86"),sQuery(id+"F50.wireOp",EDGE,"E87"),sQuery(id+"F50.wireOp",EDGE,"E85")])],"isStart":false});
            var sketch = newSketch(context, id + "F52", { "sketchPlane" : qUnion([Q0])});
            skLineSegment(sketch, "E90.top", {"start": v(-47.22, -35.86) * mm, "end": v(4.66, -35.86) * mm});
            skLineSegment(sketch, "E90.left", {"start": v(-74.28, -20) * mm, "end": v(-74.28, -24.1) * mm});
            skLineSegment(sketch, "E91", {"start": v(4.66, -35.86) * mm, "end": v(4.66, -27.87) * mm});
            skLineSegment(sketch, "E92", {"start": v(4.66, -27.87) * mm, "end": v(-34.03, -27.87) * mm});
            skLineSegment(sketch, "E93", {"start": v(-34.03, -27.87) * mm, "end": v(-34.03, -20) * mm});
            skLineSegment(sketch, "E94.top", {"start": v(-47.22, 35.86) * mm, "end": v(4.66, 35.86) * mm});
            skLineSegment(sketch, "E94.left", {"start": v(-74.28, 20) * mm, "end": v(-74.28, 23.76) * mm});
            skLineSegment(sketch, "E95", {"start": v(4.66, 35.86) * mm, "end": v(4.66, 27.87) * mm});
            skLineSegment(sketch, "E96", {"start": v(4.66, 27.87) * mm, "end": v(-34.32, 27.87) * mm});
            skLineSegment(sketch, "E97", {"start": v(-34.32, 27.87) * mm, "end": v(-34.32, 20) * mm});
            skLineSegment(sketch, "E98", {"start": v(-74.28, 23.76) * mm, "end": v(-47.22, 23.76) * mm});
            skLineSegment(sketch, "E99", {"start": v(-47.22, 23.76) * mm, "end": v(-47.22, 35.86) * mm});
            skLineSegment(sketch, "E100", {"start": v(-74.28, -24.1) * mm, "end": v(-47.22, -24.1) * mm});
            skLineSegment(sketch, "E101", {"start": v(-47.22, -24.1) * mm, "end": v(-47.22, -35.86) * mm});
            skSolve(sketch);
        }
        {
            var Q0;
            Q0=makeQuery(id+"F52.imprint","IMPRINT",FACE,{"disambiguationData":[TD([[makeQuery(id+"F52.imprint","IMPRINT",EDGE,{"derivedFrom":sQuery(id+"F52.wireOp",EDGE,"E94.top")}),-1.0]])]});
            var Q1;
            Q1=makeQuery(id+"F52.imprint","IMPRINT",FACE,{"disambiguationData":[TD([[makeQuery(id+"F52.imprint","IMPRINT",EDGE,{"derivedFrom":sQuery(id+"F52.wireOp",EDGE,"E90.top")}),1.0]])]});
            extrude(context, id + "F53", {"entities" : qUnion([Q0, Q1]), "operationType" : NewBodyOperationType.ADD, "oppositeDirection" : true, "depth" : 6 * mm});
        }
    });
